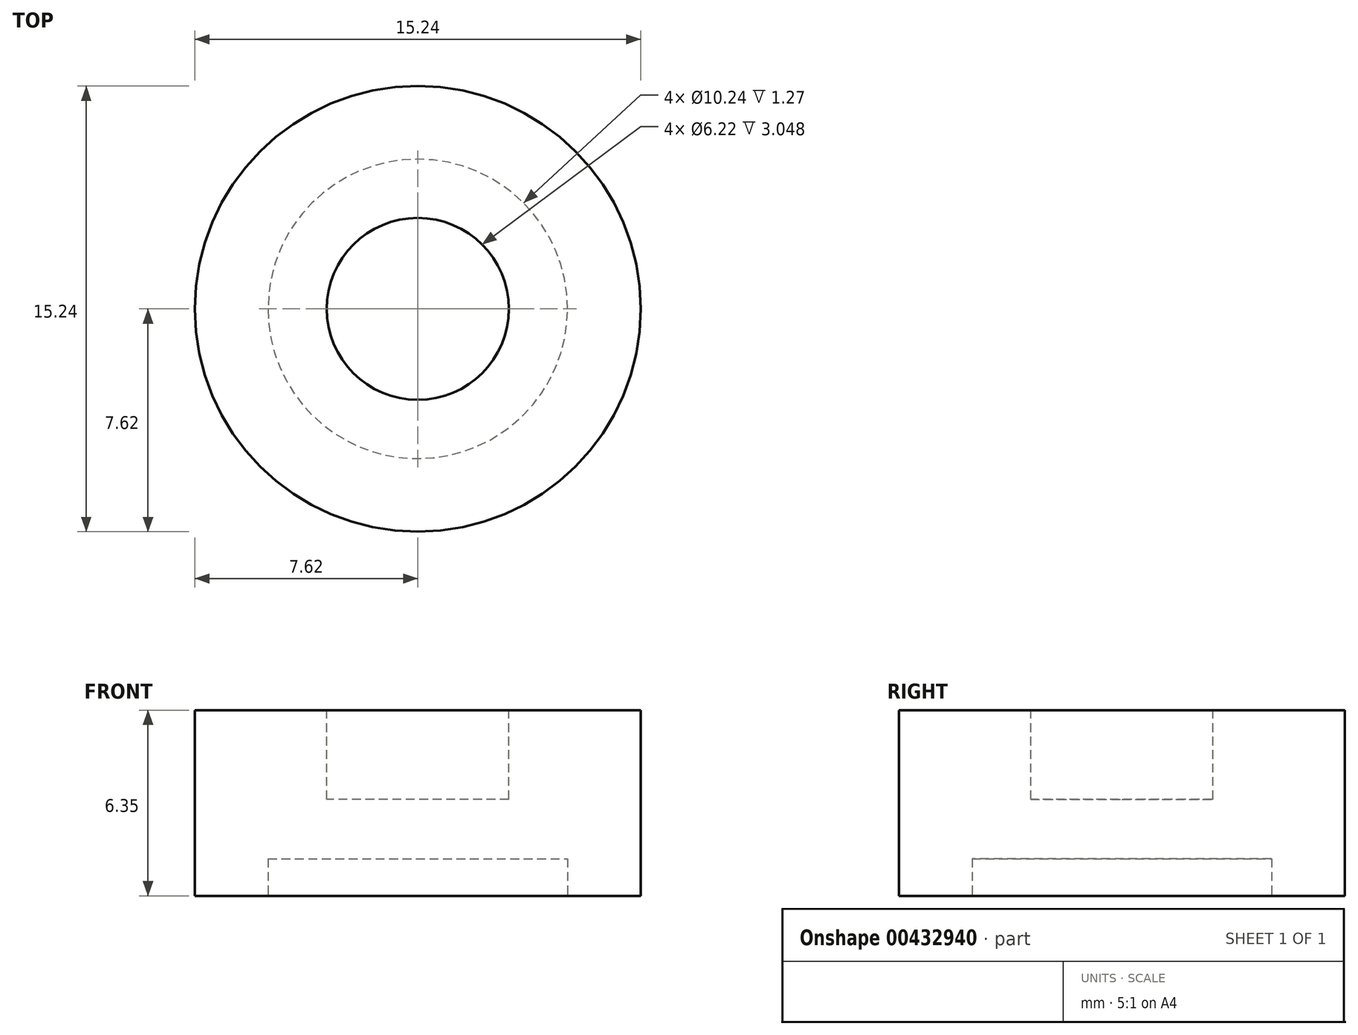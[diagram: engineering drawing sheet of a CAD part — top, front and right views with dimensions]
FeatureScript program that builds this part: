
annotation { "Feature Type Name" : "Feature", "Feature Type Description" : "" }
export const myFeature = defineFeature(function(context is Context, id is Id, definition is map)
    precondition{}
    {
        {
            var Q0;
            Q0=qCreatedBy(makeId("Top.planeOp"),FACE);
            var sketch = newSketch(context, id + "F0", { "sketchPlane" : qUnion([Q0])});
            skCircle(sketch, "E0", {"center": v(0, 0) * mm, "radius": 7.62 * mm});
            skSolve(sketch);
        }
        {
            var Q0;
            Q0=qSketchRegion(id+"F0",true);
            extrude(context, id + "F1", {"entities" : qUnion([Q0]), "depth" : 6.35 * mm});
        }
        {
            var Q0;
            Q0=makeQuery(id+"F1.opExtrude","CAP_FACE",FACE,{"disambiguationData":[OSD([sQuery(id+"F0.wireOp",EDGE,"E0")])],"isStart":true});
            var sketch = newSketch(context, id + "F2", { "sketchPlane" : qUnion([Q0])});
            skCircle(sketch, "E1", {"center": v(0, 0) * mm, "radius": 5.12 * mm});
            skSolve(sketch);
        }
        {
            var Q0;
            Q0=qSketchRegion(id+"F2",true);
            extrude(context, id + "F3", {"entities" : qUnion([Q0]), "operationType" : NewBodyOperationType.REMOVE, "oppositeDirection" : true, "depth" : 1.27 * mm});
        }
        {
            var Q0;
            Q0=makeQuery(id+"F1.opExtrude","CAP_FACE",FACE,{"disambiguationData":[OSD([sQuery(id+"F0.wireOp",EDGE,"E0")])],"isStart":false});
            var sketch = newSketch(context, id + "F4", { "sketchPlane" : qUnion([Q0])});
            skCircle(sketch, "E2", {"center": v(0, 0) * mm, "radius": 3.11 * mm});
            skSolve(sketch);
        }
        {
            var Q0;
            Q0=qSketchRegion(id+"F4",true);
            extrude(context, id + "F5", {"entities" : qUnion([Q0]), "operationType" : NewBodyOperationType.REMOVE, "oppositeDirection" : true, "depth" : 3.05 * mm});
        }
    });
